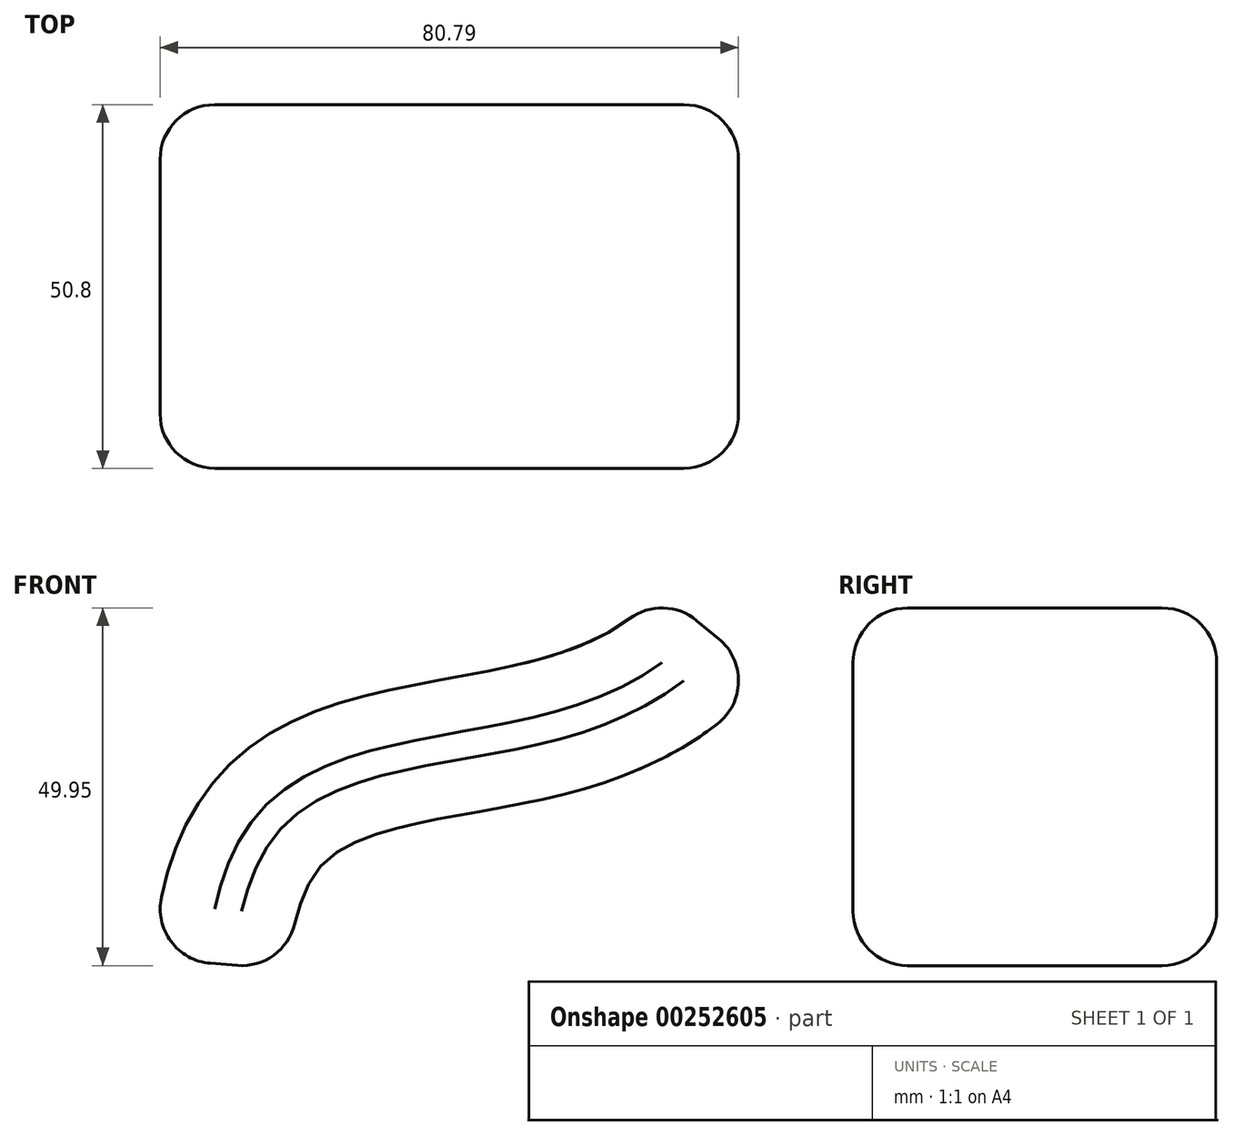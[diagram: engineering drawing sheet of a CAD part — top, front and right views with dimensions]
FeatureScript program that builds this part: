
annotation { "Feature Type Name" : "Feature", "Feature Type Description" : "" }
export const myFeature = defineFeature(function(context is Context, id is Id, definition is map)
    precondition{}
    {
        {
            var Q0;
            Q0=qCreatedBy(makeId("Front.planeOp"),FACE);
            var sketch = newSketch(context, id + "F0", { "sketchPlane" : qUnion([Q0])});
            skFitSpline(sketch, "E0", {"points": [v(-32.4, -29.19) * mm, v(38.46, 22.29) * mm], "startDerivative": vector(12.48, 154.12) * mm, "endDerivative": vector(53.98, 65.29) * mm});
            skFitSpline(sketch, "E1.0", {"points": [v(-13.41, -30.72) * mm, v(-13.21, -28.28) * mm, v(-12.74, -25.19) * mm, v(-11.9, -22.07) * mm, v(-11.24, -20.19) * mm, v(-10.55, -18.71) * mm, v(-9.87, -17.55) * mm, v(-9.2, -16.63) * mm, v(-8.52, -15.86) * mm, v(-7.77, -15.17) * mm, v(-6.91, -14.52) * mm, v(-5.9, -13.87) * mm, v(-4.27, -13.02) * mm, v(-1.69, -11.97) * mm, v(2.32, -10.81) * mm, v(7.12, -9.77) * mm, v(12.57, -8.77) * mm, v(18.57, -7.68) * mm, v(25.03, -6.27) * mm, v(30.78, -4.6) * mm, v(35.56, -2.74) * mm, v(39.2, -1.04) * mm, v(42.87, 1.05) * mm, v(46.48, 3.58) * mm, v(49.96, 6.59) * mm, v(52.12, 8.91) * mm, v(53.15, 10.15) * mm]});
            skLineSegment(sketch, "E2", {"start": v(38.46, 22.29) * mm, "end": v(53.15, 10.15) * mm});
            skLineSegment(sketch, "E3", {"start": v(-32.4, -29.19) * mm, "end": v(-13.41, -30.72) * mm});
            skSolve(sketch);
        }
        {
            var Q0;
            Q0=makeQuery(id+"F0.imprint","IMPRINT",FACE,{"disambiguationData":[TD([[makeQuery(id+"F0.imprint","IMPRINT",EDGE,{"derivedFrom":sQuery(id+"F0.wireOp",EDGE,"E0")}),-1.0]])]});
            extrude(context, id + "F1", {"entities" : qUnion([Q0]), "depth" : 50.8 * mm});
        }
        {
            var Q0;
            Q0=makeQuery(id+"F1.opExtrude","SWEPT_EDGE",EDGE,{"disambiguationData":[OSD([sQuery(id+"F0.wireOp",EDGE,"E0"),sQuery(id+"F0.wireOp",EDGE,"E2")])]});
            var Q1;
            Q1=makeQuery(id+"F1.opExtrude","CAP_EDGE",EDGE,{"disambiguationData":[OSD([sQuery(id+"F0.wireOp",EDGE,"E2")])],"isStart":false});
            var Q2;
            Q2=makeQuery(id+"F1.opExtrude","CAP_EDGE",EDGE,{"disambiguationData":[OSD([sQuery(id+"F0.wireOp",EDGE,"E2")])],"isStart":true});
            var Q3;
            Q3=makeQuery(id+"F1.opExtrude","SWEPT_EDGE",EDGE,{"disambiguationData":[OSD([sQuery(id+"F0.wireOp",EDGE,"E1.0"),sQuery(id+"F0.wireOp",EDGE,"E2")])]});
            var Q4;
            Q4=makeQuery(id+"F1.opExtrude","CAP_FACE",FACE,{"disambiguationData":[OSD([sQuery(id+"F0.wireOp",EDGE,"E0"),sQuery(id+"F0.wireOp",EDGE,"E1.0"),sQuery(id+"F0.wireOp",EDGE,"E2"),sQuery(id+"F0.wireOp",EDGE,"E3")])],"isStart":false});
            var Q5;
            Q5=makeQuery(id+"F1.opExtrude","SWEPT_FACE",FACE,{"disambiguationData":[OSD([sQuery(id+"F0.wireOp",EDGE,"E3")])]});
            var Q6;
            Q6=makeQuery(id+"F1.opExtrude","SWEPT_FACE",FACE,{"disambiguationData":[OSD([sQuery(id+"F0.wireOp",EDGE,"E1.0")])]});
            var Q7;
            Q7=makeQuery(id+"F1.opExtrude","CAP_FACE",FACE,{"disambiguationData":[OSD([sQuery(id+"F0.wireOp",EDGE,"E0"),sQuery(id+"F0.wireOp",EDGE,"E1.0"),sQuery(id+"F0.wireOp",EDGE,"E2"),sQuery(id+"F0.wireOp",EDGE,"E3")])],"isStart":true});
            fillet(context, id + "F2", {"entities" : qUnion([Q0, Q1, Q2, Q3, Q4, Q5, Q6, Q7]), "radius" : 7.62 * mm, "tangentPropagation" : true, "allowEdgeOverflow" : false});
        }
    });
